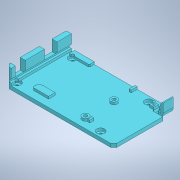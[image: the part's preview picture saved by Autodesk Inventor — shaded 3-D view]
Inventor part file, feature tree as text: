
AUTODESK INVENTOR PART (.ipt)
format: ipt  version: 2022.5 (Build 265521000, 521)  size: 427,008 bytes
history: native  units: in
note: dims shown in document units (in); Inventor stores cm internally (conversion verified against a paired STEP export)
features: sketch x12, extrude x11, reference x4, other x3
ambient origin geometry x8: Origin, YZ Plane, XZ Plane, XY Plane, X Axis, Y Axis, Z Axis, Center Point
bodies: Solid1 (feature_tree)
feature tree (30):
  other  "Arduino mega 2560.ipt"
  sketch  "Sketch: base_"  dims[d3=2.0965in d4=0.0394in d6=0.4626in]
  sketch  "Sketch: front wall"  dims[d8=0.1in d12=0.2008in]
  sketch  "Sketch: front power wall"  dims[d14=0.05in d15=0.0925in d16=0.0394in d17=0.0394in]
  sketch  "Sketch: hole popup"  dims[d20=0.0945in d21=0.3425in]
  sketch  "Sketch: prop up"  dims[d23=0.3031in d24=0.1024in]
  sketch  "Sketch: front wall cutout"  dims[d25=0.565in d26=0.6063in]
  extrude  "Ex: base"  Depth=0.0394in
  extrude  "Ex: front wall build"  Depth=0.0394in
  extrude  "Ex: front wall cut"  Depth=0.2008in
  extrude  "Ex: hole popup1"  Depth=0.0394in
  extrude  "Ex: hole popup2"  Depth=0.0945in
  extrude  "Ex: prop up"  Depth=0.1024in
  extrude  "Ex: front wall cutout"  Depth=0.6063in
  sketch  "Sketch: ramp"  dims[d27=0.0945in d28=0.6929in]
  extrude  "Ex: ramp"  Depth=0.0945in
  extrude  "Ex: ramp cutout"  Depth=3.8898in
  extrude  "Ex: countersink for standoffs"  Depth=1.5079in
  extrude  "Ex: holes for mounting"  Depth=0.1in
  sketch  "Sketch: base"  dims[d29=1.3898in d30=3.8898in]
  sketch  "Sketch: power"  dims[d31=3.9961in d32=1.5079in]
  sketch  "Sketch: pins"  dims[d33=0.1063in d34=0.1in]
  sketch  "Sketch: mounting to PCB Arduino"  dims[d35=1.2854in d36=0.6457in d37=0.4764in d38=0.3642in d39=0.25in d40=0.561in d41=0.3504in d42=0.0846in d43=0.7579in d44=0.4429in d46=0.4311in d48=0.065in d49=0.0in d50=0.4291in d52=0.4941in d53=0.0984in d54=0.1969in d55=1.8209in d56=0.0394in d57=0.1476in d58=0.0394in d59=0.0394in d60=2.6181in d61=0.3248in d62=0.1929in d63=2.7795in d64=0.4193in d65=0.0in d66=0.0492in d67=0.0in d68=0.2933in d69=0.1969in d70=1.3917in d71=1.1909in d72=0.1969in d73=0.2933in d74=0.3366in d75=0.1083in d76=0.4567in d78=0.5807in d79=0.4449in d80=0.0492in d81=0.0in d82=0.1969in d83=0.1969in d84=0.6102in d85=0.2953in d86=0.0787in d87=0.2559in d2=135.0deg d5=0.0394in d7=135.0deg d9=0.1181in d10=135.0deg d11=0.1181in d13=4.1439in d18=2.3189in d19=0.0394in d22=0.0364in d45=0.1378in d47=0.0in d51=0.374in d88=0.4921in d89=0.7244in d94=0.1732in d95=0.0906in d96=0.2323in d97=0.0in d98=0.3307in d99=0.0in d100=0.1299in d101=0.2539in d103=0.0394in d104=135.0deg d105=0.5807in d106=0.2124in d107=0.2352in d108=0.126in d110=0.0787in d111=0.1575in d113=0.2323in d114=0.0in d115=0.0787in d116=0.2362in d118=0.2539in d119=0.128in d121=0.3766in d122=135.0deg d124=0.0551in d125=0.0in d126=0.0in d127=135.0deg d128=0.1575in d129=0.7579in d130=0.0394in d131=0.2805in d132=0.3577in d134=0.0205in d135=0.1496in d136=0.0955in d138=0.1348in d139=0.1388in d140=0.565in d141=135.0deg d142=135.0deg d143=0.0394in d144=0.1181in d145=0.7244in d146=0.0in d148=0.0in d149=0.0in d150=0.2323in d151=0.5669in d152=0.0787in d153=0.1969in d154=0.2972in d155=0.0298in d156=0.7382in d157=0.0866in d158=0.0866in d159=0.1732in d160=0.2559in d161=0.0394in d162=135.0deg d163=0.7283in d164=0.3386in d165=0.2697in d166=0.0591in d168=0.0984in d169=0.0593in d170=0.1041in d171=0.0689in d172=0.0177in d173=0.1577in d175=0.0945in d176=0.3937in d177=0.0in d178=0.3937in d179=0.0in d180=0.0573in d181=0.0039in d183=0.0059in d184=0.0315in d185=0.3937in d186=0.3819in d187=0.1299in d190=0.3in d191=0.1083in d192=0.0in d193=0.0in d194=0.0in d195=0.0175in d196=0.1693in d197=0.1634in d188=0.0344in d189=0.0197in d198=0.0197in d199=0.0344in d200=0.0197in d201=0.0344in]
  reference  "Reference1"
  reference  "Reference2"
  reference  "Reference3"
  reference  "Reference4"
  sketch  "Sketch15"  dims[d0=0.3937in d1=0.0394in]
  other  "Assembly1.iam"
  other  "Arduino mega 2560:2"
